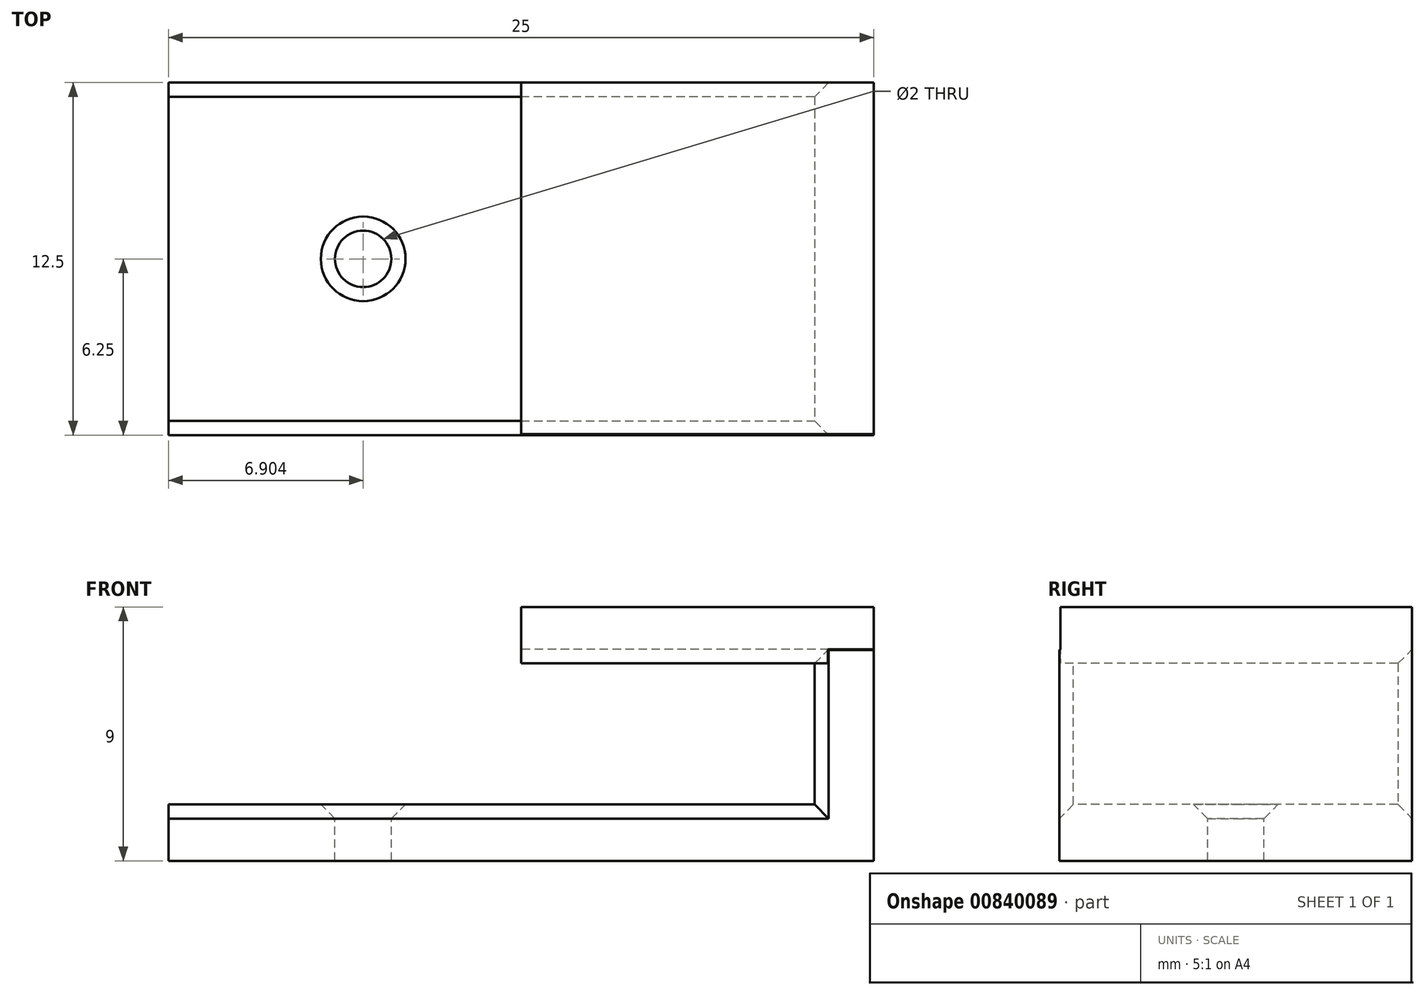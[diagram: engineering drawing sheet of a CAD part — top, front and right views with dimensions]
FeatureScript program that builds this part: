
annotation { "Feature Type Name" : "Feature", "Feature Type Description" : "" }
export const myFeature = defineFeature(function(context is Context, id is Id, definition is map)
    precondition{}
    {
        {
            var Q0;
            Q0=qCreatedBy(makeId("Top.planeOp"),FACE);
            var sketch = newSketch(context, id + "F0", { "sketchPlane" : qUnion([Q0])});
            skLineSegment(sketch, "E0.bottom", {"start": v(12.5, 6.25) * mm, "end": v(-12.5, 6.25) * mm});
            skLineSegment(sketch, "E0.top", {"start": v(12.5, -6.25) * mm, "end": v(-12.5, -6.25) * mm});
            skLineSegment(sketch, "E0.left", {"start": v(12.5, 6.25) * mm, "end": v(12.5, -6.25) * mm});
            skLineSegment(sketch, "E0.right", {"start": v(-12.5, 6.25) * mm, "end": v(-12.5, -6.25) * mm});
            skPoint(sketch, "E0.middle", {"position": v(0, 0) * mm});
            skSolve(sketch);
        }
        {
            var Q0;
            Q0 = qSketchRegion(id + "F0", true);
            extrude(context, id + "F1", {"entities" : qUnion([Q0]), "depth" : 2 * mm, "offsetDistance" : 25 * mm});
        }
        {
            var Q0;
            Q0=makeQuery(id+"F1.opExtrude","CAP_FACE",FACE,{"disambiguationData":[OSD([sQuery(id+"F0.wireOp",EDGE,"E0.bottom"),sQuery(id+"F0.wireOp",EDGE,"E0.top"),sQuery(id+"F0.wireOp",EDGE,"E0.left"),sQuery(id+"F0.wireOp",EDGE,"E0.right")])],"isStart":false});
            var sketch = newSketch(context, id + "F2", { "sketchPlane" : qUnion([Q0])});
            skLineSegment(sketch, "E1.bottom", {"start": v(12.5, 6.25) * mm, "end": v(10.4, 6.25) * mm});
            skLineSegment(sketch, "E1.top", {"start": v(12.5, -6.25) * mm, "end": v(10.4, -6.25) * mm});
            skLineSegment(sketch, "E1.left", {"start": v(12.5, 6.25) * mm, "end": v(12.5, -6.25) * mm});
            skLineSegment(sketch, "E1.right", {"start": v(10.4, 6.25) * mm, "end": v(10.4, -6.25) * mm});
            skSolve(sketch);
        }
        {
            var Q0;
            Q0 = qSketchRegion(id + "F2", true);
            extrude(context, id + "F3", {"entities" : qUnion([Q0]), "operationType" : NewBodyOperationType.ADD, "depth" : 5 * mm, "offsetDistance" : 25 * mm});
        }
        {
            var Q0;
            Q0=makeQuery(id+"F3.opExtrude","CAP_FACE",FACE,{"disambiguationData":[OSD([sQuery(id+"F2.wireOp",EDGE,"E1.bottom"),sQuery(id+"F2.wireOp",EDGE,"E1.top"),sQuery(id+"F2.wireOp",EDGE,"E1.left"),sQuery(id+"F2.wireOp",EDGE,"E1.right")])],"isStart":false});
            var sketch = newSketch(context, id + "F4", { "sketchPlane" : qUnion([Q0])});
            skLineSegment(sketch, "E2.bottom", {"start": v(12.5, 6.25) * mm, "end": v(0, 6.25) * mm});
            skLineSegment(sketch, "E2.top", {"start": v(12.5, -6.32) * mm, "end": v(0, -6.32) * mm});
            skLineSegment(sketch, "E2.left", {"start": v(12.5, 6.25) * mm, "end": v(12.5, -6.32) * mm});
            skLineSegment(sketch, "E2.right", {"start": v(0, 6.25) * mm, "end": v(0, -6.32) * mm});
            skSolve(sketch);
        }
        {
            var Q0;
            Q0 = qSketchRegion(id + "F4", true);
            extrude(context, id + "F5", {"entities" : qUnion([Q0]), "operationType" : NewBodyOperationType.ADD, "depth" : 2 * mm, "offsetDistance" : 25 * mm});
        }
        {
            var Q0;
            Q0=makeQuery(id+"F3.opExtrude","SWEPT_EDGE",EDGE,{"disambiguationData":[OSD([sQuery(id+"F0.wireOp",EDGE,"E0.bottom"),sQuery(id+"F2.wireOp",EDGE,"E1.bottom"),sQuery(id+"F2.wireOp",EDGE,"E1.right")])]});
            var Q1;
            Q1=makeQuery(id+"F1.opExtrude","CAP_EDGE",EDGE,{"disambiguationData":[OSD([sQuery(id+"F0.wireOp",EDGE,"E0.bottom")])],"isStart":false});
            var Q2;
            Q2=makeQuery(id+"F3.opExtrude","SWEPT_EDGE",EDGE,{"disambiguationData":[OSD([sQuery(id+"F0.wireOp",EDGE,"E0.top"),sQuery(id+"F2.wireOp",EDGE,"E1.top"),sQuery(id+"F2.wireOp",EDGE,"E1.right")])]});
            var Q3;
            Q3=makeQuery(id+"F1.opExtrude","CAP_EDGE",EDGE,{"disambiguationData":[OSD([sQuery(id+"F0.wireOp",EDGE,"E0.top")])],"isStart":false});
            var Q4;
            Q4=makeQuery(id+"F5.opExtrude","CAP_EDGE",EDGE,{"disambiguationData":[OSD([sQuery(id+"F4.wireOp",EDGE,"E2.bottom")])],"isStart":true});
            chamfer(context, id + "F6", {"entities" : qUnion([Q0, Q1, Q2, Q3, Q4]), "width" : 0.5 * mm, "tangentPropagation" : true});
        }
        {
            var Q0;
            Q0=makeQuery(id+"F1.opExtrude","CAP_FACE",FACE,{"disambiguationData":[OSD([sQuery(id+"F0.wireOp",EDGE,"E0.bottom"),sQuery(id+"F0.wireOp",EDGE,"E0.top"),sQuery(id+"F0.wireOp",EDGE,"E0.left"),sQuery(id+"F0.wireOp",EDGE,"E0.right")])],"isStart":false});
            var sketch = newSketch(context, id + "F7", { "sketchPlane" : qUnion([Q0])});
            skCircle(sketch, "E3", {"center": v(-5.6, 0) * mm, "radius": 1.52 * mm});
            skSolve(sketch);
        }
        {
            var Q0;
            Q0=sQuery(id+"F7.wireOp",VERTEX,"E3.center");
            var Q1;
            Q1=makeQuery(id+"F1.opExtrude","SWEPT_BODY",BODY,{"disambiguationData":[OSD([sQuery(id+"F0.wireOp",EDGE,"E0.bottom"),sQuery(id+"F0.wireOp",EDGE,"E0.top"),sQuery(id+"F0.wireOp",EDGE,"E0.left"),sQuery(id+"F0.wireOp",EDGE,"E0.right")])]});
            hole(context, id + "F8", {"style" : HoleStyle.C_SINK, "endStyle" : HoleEndStyle.THROUGH, "holeDiameter" : 2 * mm, "cSinkDiameter" : 3 * mm, "cSinkAngle" : 90 * degree, "majorDiameter" : 5 * mm, "isTappedThrough" : true, "tappedDepth" : 12 * mm, "tapClearance" : 3, "locations" : qUnion([Q0]), "scope" : qUnion([Q1])});
        }
        {
            var Q0;
            Q0=makeQuery(id+"F5.opExtrude","SWEPT_FACE",FACE,{"disambiguationData":[OSD([sQuery(id+"F4.wireOp",EDGE,"E2.top")])]});
            extrude(context, id + "F9", {"entities" : qUnion([Q0]), "operationType" : NewBodyOperationType.REMOVE, "oppositeDirection" : true, "depth" : 0.1 * mm, "offsetDistance" : 25 * mm});
        }
        {
            var Q0;
            {var subQ0=sQuery(id+"F4.wireOp",EDGE,"E2.top");Q0=makeQuery(id+"F9.boolean.opBoolean","COPY",EDGE,{"disambiguationData":[topologyDisambiguationEdgeConnected([makeQuery(id+"F5.opExtrude","CAP_FACE",FACE,{"disambiguationData":[OSD([sQuery(id+"F4.wireOp",EDGE,"E2.bottom"),subQ0,sQuery(id+"F4.wireOp",EDGE,"E2.left"),sQuery(id+"F4.wireOp",EDGE,"E2.right")])],"isStart":true})])],"derivedFrom":makeQuery(id+"F9.opExtrude","CAP_EDGE",EDGE,{"disambiguationData":[OSD([subQ0]),TDD([makeQuery(id+"F5.opExtrude","CAP_EDGE",EDGE,{"disambiguationData":[OSD([subQ0])],"isStart":true})])],"isStart":false})});}
            chamfer(context, id + "F10", {"entities" : qUnion([Q0]), "width" : 0.5 * mm, "tangentPropagation" : true});
        }
    });
